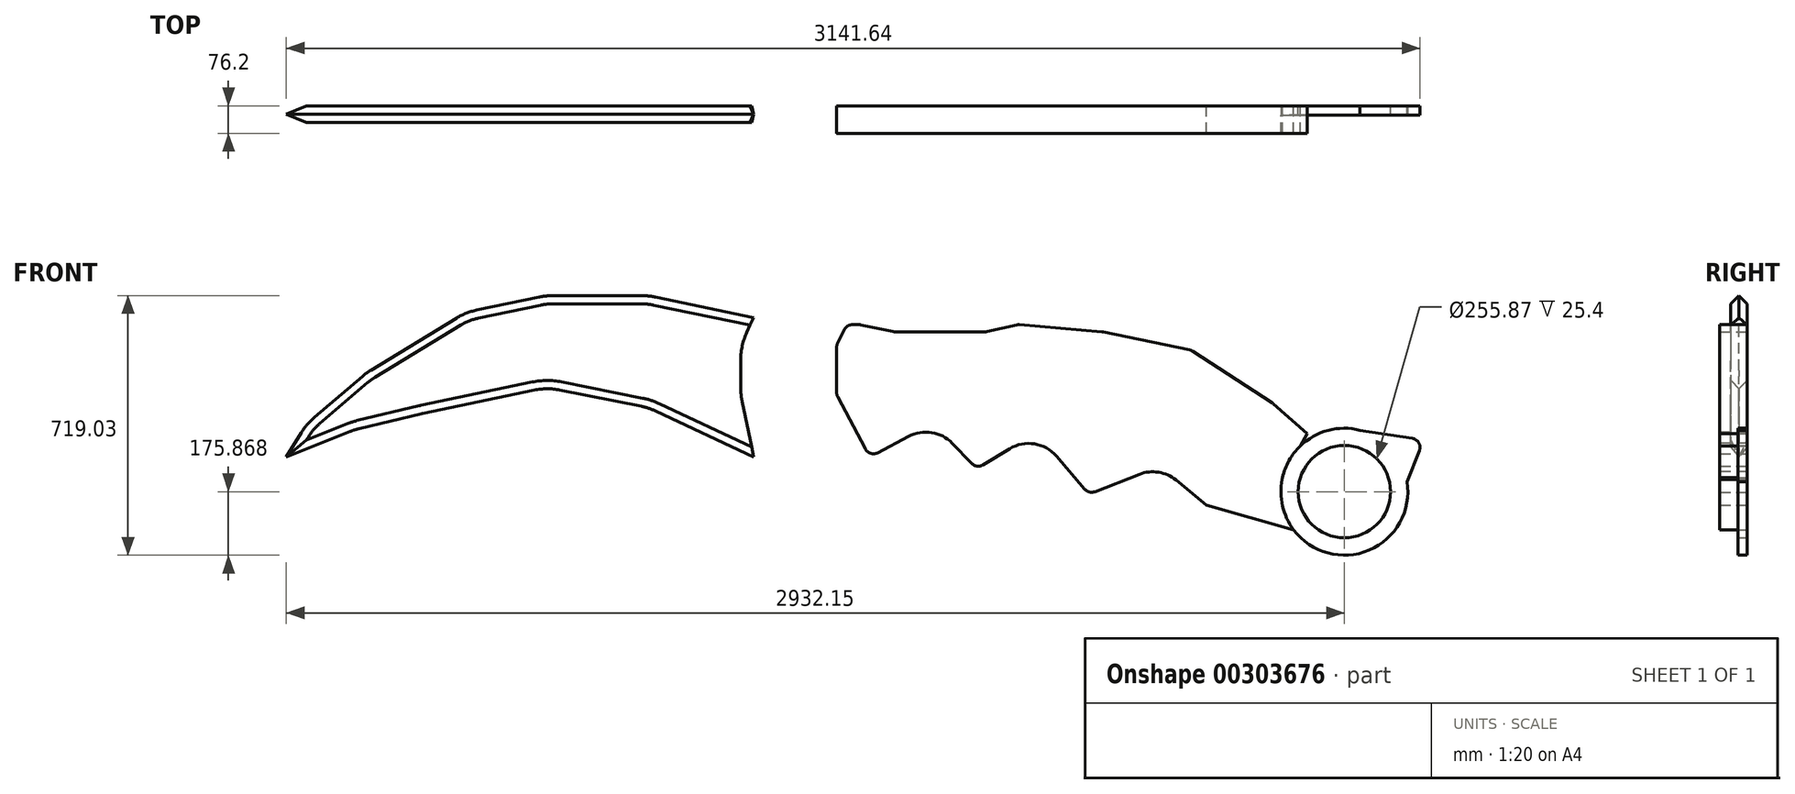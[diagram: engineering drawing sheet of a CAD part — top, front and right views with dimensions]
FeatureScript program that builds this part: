
annotation { "Feature Type Name" : "Feature", "Feature Type Description" : "" }
export const myFeature = defineFeature(function(context is Context, id is Id, definition is map)
    precondition{}
    {
        {
            var Q0;
            Q0=qCreatedBy(makeId("Front.planeOp"),FACE);
            var sketch = newSketch(context, id + "F0", { "sketchPlane" : qUnion([Q0])});
            skLineSegment(sketch, "E0", {"start": v(-453.29, 120.3) * mm, "end": v(-106.22, 192.94) * mm});
            skLineSegment(sketch, "E1", {"start": v(-106.22, 192.94) * mm, "end": v(176.28, 136.44) * mm});
            skLineSegment(sketch, "E2", {"start": v(176.28, 136.44) * mm, "end": v(466.85, 0) * mm});
            skLineSegment(sketch, "E3", {"start": v(466.85, 0) * mm, "end": v(430.81, 172.16) * mm});
            skLineSegment(sketch, "E4", {"start": v(430.81, 172.16) * mm, "end": v(430.81, 309.97) * mm});
            skLineSegment(sketch, "E5", {"start": v(430.81, 309.97) * mm, "end": v(466.85, 386.71) * mm});
            skLineSegment(sketch, "E6", {"start": v(466.85, 386.71) * mm, "end": v(176.28, 447.19) * mm});
            skLineSegment(sketch, "E7", {"start": v(176.28, 447.19) * mm, "end": v(-110.25, 447.19) * mm});
            skLineSegment(sketch, "E8", {"start": v(-110.25, 447.19) * mm, "end": v(-331, 400.99) * mm});
            skLineSegment(sketch, "E9", {"start": v(-331, 400.99) * mm, "end": v(-606.64, 233.3) * mm});
            skLineSegment(sketch, "E10", {"start": v(-606.64, 233.3) * mm, "end": v(-772.1, 92.05) * mm});
            skLineSegment(sketch, "E11", {"start": v(-453.29, 120.3) * mm, "end": v(-638.93, 75.9) * mm});
            skLineSegment(sketch, "E12", {"start": v(-638.93, 75.9) * mm, "end": v(-828.6, 0) * mm});
            skLineSegment(sketch, "E13", {"start": v(-828.6, 0) * mm, "end": v(-772.1, 92.05) * mm});
            skLineSegment(sketch, "E14", {"start": v(760.34, 366.98) * mm, "end": v(854.97, 347.29) * mm});
            skLineSegment(sketch, "E15", {"start": v(854.97, 347.29) * mm, "end": v(1111.8, 347.29) * mm});
            skLineSegment(sketch, "E16", {"start": v(1198.7, 366.98) * mm, "end": v(1111.8, 347.29) * mm});
            skLineSegment(sketch, "E17", {"start": v(1198.7, 366.98) * mm, "end": v(1433.47, 347.29) * mm});
            skLineSegment(sketch, "E18", {"start": v(1433.47, 347.29) * mm, "end": v(1678.72, 296.25) * mm});
            skLineSegment(sketch, "E19", {"start": v(1678.72, 296.25) * mm, "end": v(1905.09, 149.09) * mm});
            skLineSegment(sketch, "E20", {"start": v(1905.09, 149.09) * mm, "end": v(2000.28, 64.3) * mm});
            skLineSegment(sketch, "E21", {"start": v(2046.94, -225.32) * mm, "end": v(1721.16, -132.66) * mm});
            skLineSegment(sketch, "E22", {"start": v(1721.16, -132.66) * mm, "end": v(1591.06, -26.27) * mm});
            skLineSegment(sketch, "E23", {"start": v(1591.06, -26.27) * mm, "end": v(1395.4, -102.36) * mm});
            skLineSegment(sketch, "E24", {"start": v(1395.4, -102.36) * mm, "end": v(1249.48, 67.78) * mm});
            skLineSegment(sketch, "E25", {"start": v(1249.48, 67.78) * mm, "end": v(1084.9, -32.14) * mm});
            skLineSegment(sketch, "E26", {"start": v(1084.9, -32.14) * mm, "end": v(963.65, 93.24) * mm});
            skLineSegment(sketch, "E27", {"start": v(963.65, 93.24) * mm, "end": v(788, 0) * mm});
            skLineSegment(sketch, "E28", {"start": v(788, 0) * mm, "end": v(696.61, 172.16) * mm});
            skLineSegment(sketch, "E29", {"start": v(696.61, 172.16) * mm, "end": v(696.61, 309.97) * mm});
            skLineSegment(sketch, "E30", {"start": v(696.61, 309.97) * mm, "end": v(724.68, 366.98) * mm});
            skLineSegment(sketch, "E31", {"start": v(724.68, 366.98) * mm, "end": v(760.34, 366.98) * mm});
            skLineSegment(sketch, "E32", {"start": v(2000.28, 64.3) * mm, "end": v(1929.8, -60.84) * mm});
            skLineSegment(sketch, "E33", {"start": v(1929.8, -60.84) * mm, "end": v(2046.94, -225.32) * mm});
            skCircle(sketch, "E34", {"center": v(2103.54, -95.97) * mm, "radius": 175.87 * mm});
            skCircle(sketch, "E35", {"center": v(2103.54, -95.97) * mm, "radius": 127.93 * mm});
            skLineSegment(sketch, "E36", {"start": v(2146.97, 74.45) * mm, "end": v(2322.95, 46.97) * mm});
            skLineSegment(sketch, "E37", {"start": v(2322.95, 46.97) * mm, "end": v(2277.24, -68.42) * mm});
            skSolve(sketch);
        }
        {
            var Q0;
            Q0=makeQuery(id+"F0.imprint","IMPRINT",FACE,{"disambiguationData":[TD([[makeQuery(id+"F0.imprint","IMPRINT",EDGE,{"derivedFrom":sQuery(id+"F0.wireOp",EDGE,"E0")}),1.0]])]});
            extrude(context, id + "F1", {"entities" : qUnion([Q0]), "depth" : 45.72 * mm});
        }
        {
            var Q0;
            {var subQ0=sQuery(id+"F0.wireOp",EDGE,"E36");Q0=makeQuery(id+"F0.imprint","IMPRINT",FACE,{"disambiguationData":[TD([[makeQuery(id+"F0.imprint","IMPRINT",EDGE,{"derivedFrom":subQ0}),-1.0]])]});}
            var Q1;
            {var subQ1=sQuery(id+"F0.wireOp",EDGE,"E21");var subQ3=sQuery(id+"F0.wireOp",EDGE,"E33");var subQ5=makeQuery(id+"F0.imprint","INTERSECT",VERTEX,{"derivedFrom":[subQ1,subQ3]});Q1=makeQuery(id+"F0.imprint","IMPRINT",FACE,{"disambiguationData":[TD([[makeQuery(id+"F0.imprint","IMPRINT",EDGE,{"disambiguationData":[TD([[subQ5,-1.0]])],"derivedFrom":subQ1}),-1.0]])]});}
            var Q2;
            {var subQ1=sQuery(id+"F0.wireOp",EDGE,"E33");var subQ5=sQuery(id+"F0.wireOp",EDGE,"E21");var subQ6=makeQuery(id+"F0.imprint","INTERSECT",VERTEX,{"derivedFrom":[subQ5,subQ1]});Q2=makeQuery(id+"F0.imprint","IMPRINT",FACE,{"disambiguationData":[TD([[makeQuery(id+"F0.imprint","IMPRINT",EDGE,{"disambiguationData":[TD([[subQ6,-1.0]])],"derivedFrom":subQ5}),1.0]])]});}
            var Q3;
            {var subQ0=sQuery(id+"F0.wireOp",EDGE,"E34");var subQ1=sQuery(id+"F0.wireOp",EDGE,"E32");var subQ2=makeQuery(id+"F0.imprint","INTERSECT",VERTEX,{"disambiguationData":[OD(0.0)],"derivedFrom":[subQ1,subQ0]});Q3=makeQuery(id+"F0.imprint","IMPRINT",FACE,{"disambiguationData":[TD([[makeQuery(id+"F0.imprint","IMPRINT",EDGE,{"disambiguationData":[TD([[subQ2,-1.0]])],"derivedFrom":subQ1}),-1.0]])]});}
            extrude(context, id + "F2", {"entities" : qUnion([Q0, Q1, Q2, Q3]), "depth" : 25.4 * mm});
        }
        {
            var Q0;
            Q0=makeQuery(id+"F0.imprint","IMPRINT",FACE,{"disambiguationData":[TD([[makeQuery(id+"F0.imprint","IMPRINT",EDGE,{"derivedFrom":sQuery(id+"F0.wireOp",EDGE,"E14")}),-1.0]])]});
            extrude(context, id + "F3", {"entities" : qUnion([Q0]), "operationType" : NewBodyOperationType.ADD, "depth" : 76.2 * mm});
        }
        {
            var Q0;
            Q0=makeQuery(id+"F1.opExtrude","SWEPT_EDGE",EDGE,{"disambiguationData":[OSD([sQuery(id+"F0.wireOp",EDGE,"E11"),sQuery(id+"F0.wireOp",EDGE,"E12")])]});
            var Q1;
            Q1=makeQuery(id+"F1.opExtrude","SWEPT_EDGE",EDGE,{"disambiguationData":[OSD([sQuery(id+"F0.wireOp",EDGE,"E0"),sQuery(id+"F0.wireOp",EDGE,"E11")])]});
            var Q2;
            Q2=makeQuery(id+"F1.opExtrude","SWEPT_EDGE",EDGE,{"disambiguationData":[OSD([sQuery(id+"F0.wireOp",EDGE,"E0"),sQuery(id+"F0.wireOp",EDGE,"E1")])]});
            var Q3;
            Q3=makeQuery(id+"F1.opExtrude","SWEPT_EDGE",EDGE,{"disambiguationData":[OSD([sQuery(id+"F0.wireOp",EDGE,"E1"),sQuery(id+"F0.wireOp",EDGE,"E2")])]});
            var Q4;
            Q4=makeQuery(id+"F1.opExtrude","SWEPT_EDGE",EDGE,{"disambiguationData":[OSD([sQuery(id+"F0.wireOp",EDGE,"E3"),sQuery(id+"F0.wireOp",EDGE,"E4")])]});
            var Q5;
            Q5=makeQuery(id+"F1.opExtrude","SWEPT_EDGE",EDGE,{"disambiguationData":[OSD([sQuery(id+"F0.wireOp",EDGE,"E4"),sQuery(id+"F0.wireOp",EDGE,"E5")])]});
            var Q6;
            Q6=makeQuery(id+"F1.opExtrude","SWEPT_EDGE",EDGE,{"disambiguationData":[OSD([sQuery(id+"F0.wireOp",EDGE,"E6"),sQuery(id+"F0.wireOp",EDGE,"E7")])]});
            var Q7;
            Q7=makeQuery(id+"F1.opExtrude","SWEPT_EDGE",EDGE,{"disambiguationData":[OSD([sQuery(id+"F0.wireOp",EDGE,"E7"),sQuery(id+"F0.wireOp",EDGE,"E8")])]});
            var Q8;
            Q8=makeQuery(id+"F1.opExtrude","SWEPT_EDGE",EDGE,{"disambiguationData":[OSD([sQuery(id+"F0.wireOp",EDGE,"E8"),sQuery(id+"F0.wireOp",EDGE,"E9")])]});
            var Q9;
            Q9=makeQuery(id+"F1.opExtrude","SWEPT_EDGE",EDGE,{"disambiguationData":[OSD([sQuery(id+"F0.wireOp",EDGE,"E9"),sQuery(id+"F0.wireOp",EDGE,"E10")])]});
            var Q10;
            Q10=makeQuery(id+"F1.opExtrude","SWEPT_EDGE",EDGE,{"disambiguationData":[OSD([sQuery(id+"F0.wireOp",EDGE,"E10"),sQuery(id+"F0.wireOp",EDGE,"E13")])]});
            fillet(context, id + "F4", {"entities" : qUnion([Q0, Q1, Q2, Q3, Q4, Q5, Q6, Q7, Q8, Q9, Q10]), "radius" : 177.8 * mm, "tangentPropagation" : true, "allowEdgeOverflow" : false});
        }
        {
            var Q0;
            Q0=makeQuery(id+"F1.opExtrude","CAP_EDGE",EDGE,{"disambiguationData":[OSD([sQuery(id+"F0.wireOp",EDGE,"E2")])],"isStart":false});
            var Q1;
            {var subQ0=sQuery(id+"F0.wireOp",EDGE,"E2");var subQ1=sQuery(id+"F0.wireOp",EDGE,"E1");Q1=makeQuery(id+"F4.opFillet","BLEND_EDGE",EDGE,{"blendedFrom":[makeQuery(id+"F1.opExtrude","SWEPT_EDGE",EDGE,{"disambiguationData":[OSD([subQ1,subQ0])]}),makeQuery(id+"F1.opExtrude","CAP_FACE",FACE,{"disambiguationData":[OSD([sQuery(id+"F0.wireOp",EDGE,"E0"),subQ1,subQ0,sQuery(id+"F0.wireOp",EDGE,"E3"),sQuery(id+"F0.wireOp",EDGE,"E4"),sQuery(id+"F0.wireOp",EDGE,"E5"),sQuery(id+"F0.wireOp",EDGE,"E6"),sQuery(id+"F0.wireOp",EDGE,"E7"),sQuery(id+"F0.wireOp",EDGE,"E8"),sQuery(id+"F0.wireOp",EDGE,"E9"),sQuery(id+"F0.wireOp",EDGE,"E10"),sQuery(id+"F0.wireOp",EDGE,"E11"),sQuery(id+"F0.wireOp",EDGE,"E12"),sQuery(id+"F0.wireOp",EDGE,"E13")])],"isStart":false})],"blendedInto":[makeQuery(id+"F1.opExtrude","CAP_FACE",FACE,{"disambiguationData":[OSD([sQuery(id+"F0.wireOp",EDGE,"E0"),subQ1,subQ0,sQuery(id+"F0.wireOp",EDGE,"E3"),sQuery(id+"F0.wireOp",EDGE,"E4"),sQuery(id+"F0.wireOp",EDGE,"E5"),sQuery(id+"F0.wireOp",EDGE,"E6"),sQuery(id+"F0.wireOp",EDGE,"E7"),sQuery(id+"F0.wireOp",EDGE,"E8"),sQuery(id+"F0.wireOp",EDGE,"E9"),sQuery(id+"F0.wireOp",EDGE,"E10"),sQuery(id+"F0.wireOp",EDGE,"E11"),sQuery(id+"F0.wireOp",EDGE,"E12"),sQuery(id+"F0.wireOp",EDGE,"E13")])],"isStart":false})]});}
            var Q2;
            Q2=makeQuery(id+"F1.opExtrude","CAP_EDGE",EDGE,{"disambiguationData":[OSD([sQuery(id+"F0.wireOp",EDGE,"E1")])],"isStart":false});
            var Q3;
            Q3=makeQuery(id+"F1.opExtrude","CAP_EDGE",EDGE,{"disambiguationData":[OSD([sQuery(id+"F0.wireOp",EDGE,"E2")])],"isStart":true});
            var Q4;
            Q4=makeQuery(id+"F1.opExtrude","CAP_EDGE",EDGE,{"disambiguationData":[OSD([sQuery(id+"F0.wireOp",EDGE,"E1")])],"isStart":true});
            var Q5;
            {var subQ0=sQuery(id+"F0.wireOp",EDGE,"E2");var subQ1=sQuery(id+"F0.wireOp",EDGE,"E1");Q5=makeQuery(id+"F4.opFillet","BLEND_EDGE",EDGE,{"blendedFrom":[makeQuery(id+"F1.opExtrude","SWEPT_EDGE",EDGE,{"disambiguationData":[OSD([subQ1,subQ0])]}),makeQuery(id+"F1.opExtrude","CAP_FACE",FACE,{"disambiguationData":[OSD([sQuery(id+"F0.wireOp",EDGE,"E0"),subQ1,subQ0,sQuery(id+"F0.wireOp",EDGE,"E3"),sQuery(id+"F0.wireOp",EDGE,"E4"),sQuery(id+"F0.wireOp",EDGE,"E5"),sQuery(id+"F0.wireOp",EDGE,"E6"),sQuery(id+"F0.wireOp",EDGE,"E7"),sQuery(id+"F0.wireOp",EDGE,"E8"),sQuery(id+"F0.wireOp",EDGE,"E9"),sQuery(id+"F0.wireOp",EDGE,"E10"),sQuery(id+"F0.wireOp",EDGE,"E11"),sQuery(id+"F0.wireOp",EDGE,"E12"),sQuery(id+"F0.wireOp",EDGE,"E13")])],"isStart":true})],"blendedInto":[makeQuery(id+"F1.opExtrude","CAP_FACE",FACE,{"disambiguationData":[OSD([sQuery(id+"F0.wireOp",EDGE,"E0"),subQ1,subQ0,sQuery(id+"F0.wireOp",EDGE,"E3"),sQuery(id+"F0.wireOp",EDGE,"E4"),sQuery(id+"F0.wireOp",EDGE,"E5"),sQuery(id+"F0.wireOp",EDGE,"E6"),sQuery(id+"F0.wireOp",EDGE,"E7"),sQuery(id+"F0.wireOp",EDGE,"E8"),sQuery(id+"F0.wireOp",EDGE,"E9"),sQuery(id+"F0.wireOp",EDGE,"E10"),sQuery(id+"F0.wireOp",EDGE,"E11"),sQuery(id+"F0.wireOp",EDGE,"E12"),sQuery(id+"F0.wireOp",EDGE,"E13")])],"isStart":true})]});}
            var Q6;
            Q6=makeQuery(id+"F1.opExtrude","CAP_EDGE",EDGE,{"disambiguationData":[OSD([sQuery(id+"F0.wireOp",EDGE,"E0")])],"isStart":false});
            var Q7;
            {var subQ0=sQuery(id+"F0.wireOp",EDGE,"E1");var subQ1=sQuery(id+"F0.wireOp",EDGE,"E0");Q7=makeQuery(id+"F4.opFillet","BLEND_EDGE",EDGE,{"blendedFrom":[makeQuery(id+"F1.opExtrude","SWEPT_EDGE",EDGE,{"disambiguationData":[OSD([subQ1,subQ0])]}),makeQuery(id+"F1.opExtrude","CAP_FACE",FACE,{"disambiguationData":[OSD([subQ1,subQ0,sQuery(id+"F0.wireOp",EDGE,"E2"),sQuery(id+"F0.wireOp",EDGE,"E3"),sQuery(id+"F0.wireOp",EDGE,"E4"),sQuery(id+"F0.wireOp",EDGE,"E5"),sQuery(id+"F0.wireOp",EDGE,"E6"),sQuery(id+"F0.wireOp",EDGE,"E7"),sQuery(id+"F0.wireOp",EDGE,"E8"),sQuery(id+"F0.wireOp",EDGE,"E9"),sQuery(id+"F0.wireOp",EDGE,"E10"),sQuery(id+"F0.wireOp",EDGE,"E11"),sQuery(id+"F0.wireOp",EDGE,"E12"),sQuery(id+"F0.wireOp",EDGE,"E13")])],"isStart":true})],"blendedInto":[makeQuery(id+"F1.opExtrude","CAP_FACE",FACE,{"disambiguationData":[OSD([subQ1,subQ0,sQuery(id+"F0.wireOp",EDGE,"E2"),sQuery(id+"F0.wireOp",EDGE,"E3"),sQuery(id+"F0.wireOp",EDGE,"E4"),sQuery(id+"F0.wireOp",EDGE,"E5"),sQuery(id+"F0.wireOp",EDGE,"E6"),sQuery(id+"F0.wireOp",EDGE,"E7"),sQuery(id+"F0.wireOp",EDGE,"E8"),sQuery(id+"F0.wireOp",EDGE,"E9"),sQuery(id+"F0.wireOp",EDGE,"E10"),sQuery(id+"F0.wireOp",EDGE,"E11"),sQuery(id+"F0.wireOp",EDGE,"E12"),sQuery(id+"F0.wireOp",EDGE,"E13")])],"isStart":true})]});}
            var Q8;
            {var subQ0=sQuery(id+"F0.wireOp",EDGE,"E1");var subQ1=sQuery(id+"F0.wireOp",EDGE,"E0");Q8=makeQuery(id+"F4.opFillet","BLEND_EDGE",EDGE,{"blendedFrom":[makeQuery(id+"F1.opExtrude","SWEPT_EDGE",EDGE,{"disambiguationData":[OSD([subQ1,subQ0])]}),makeQuery(id+"F1.opExtrude","CAP_FACE",FACE,{"disambiguationData":[OSD([subQ1,subQ0,sQuery(id+"F0.wireOp",EDGE,"E2"),sQuery(id+"F0.wireOp",EDGE,"E3"),sQuery(id+"F0.wireOp",EDGE,"E4"),sQuery(id+"F0.wireOp",EDGE,"E5"),sQuery(id+"F0.wireOp",EDGE,"E6"),sQuery(id+"F0.wireOp",EDGE,"E7"),sQuery(id+"F0.wireOp",EDGE,"E8"),sQuery(id+"F0.wireOp",EDGE,"E9"),sQuery(id+"F0.wireOp",EDGE,"E10"),sQuery(id+"F0.wireOp",EDGE,"E11"),sQuery(id+"F0.wireOp",EDGE,"E12"),sQuery(id+"F0.wireOp",EDGE,"E13")])],"isStart":false})],"blendedInto":[makeQuery(id+"F1.opExtrude","CAP_FACE",FACE,{"disambiguationData":[OSD([subQ1,subQ0,sQuery(id+"F0.wireOp",EDGE,"E2"),sQuery(id+"F0.wireOp",EDGE,"E3"),sQuery(id+"F0.wireOp",EDGE,"E4"),sQuery(id+"F0.wireOp",EDGE,"E5"),sQuery(id+"F0.wireOp",EDGE,"E6"),sQuery(id+"F0.wireOp",EDGE,"E7"),sQuery(id+"F0.wireOp",EDGE,"E8"),sQuery(id+"F0.wireOp",EDGE,"E9"),sQuery(id+"F0.wireOp",EDGE,"E10"),sQuery(id+"F0.wireOp",EDGE,"E11"),sQuery(id+"F0.wireOp",EDGE,"E12"),sQuery(id+"F0.wireOp",EDGE,"E13")])],"isStart":false})]});}
            var Q9;
            Q9=makeQuery(id+"F1.opExtrude","CAP_EDGE",EDGE,{"disambiguationData":[OSD([sQuery(id+"F0.wireOp",EDGE,"E0")])],"isStart":true});
            var Q10;
            Q10=makeQuery(id+"F1.opExtrude","CAP_EDGE",EDGE,{"disambiguationData":[OSD([sQuery(id+"F0.wireOp",EDGE,"E11")])],"isStart":true});
            var Q11;
            Q11=makeQuery(id+"F1.opExtrude","CAP_EDGE",EDGE,{"disambiguationData":[OSD([sQuery(id+"F0.wireOp",EDGE,"E11")])],"isStart":false});
            var Q12;
            {var subQ0=sQuery(id+"F0.wireOp",EDGE,"E12");var subQ1=sQuery(id+"F0.wireOp",EDGE,"E11");Q12=makeQuery(id+"F4.opFillet","BLEND_EDGE",EDGE,{"blendedFrom":[makeQuery(id+"F1.opExtrude","SWEPT_EDGE",EDGE,{"disambiguationData":[OSD([subQ1,subQ0])]}),makeQuery(id+"F1.opExtrude","CAP_FACE",FACE,{"disambiguationData":[OSD([sQuery(id+"F0.wireOp",EDGE,"E0"),sQuery(id+"F0.wireOp",EDGE,"E1"),sQuery(id+"F0.wireOp",EDGE,"E2"),sQuery(id+"F0.wireOp",EDGE,"E3"),sQuery(id+"F0.wireOp",EDGE,"E4"),sQuery(id+"F0.wireOp",EDGE,"E5"),sQuery(id+"F0.wireOp",EDGE,"E6"),sQuery(id+"F0.wireOp",EDGE,"E7"),sQuery(id+"F0.wireOp",EDGE,"E8"),sQuery(id+"F0.wireOp",EDGE,"E9"),sQuery(id+"F0.wireOp",EDGE,"E10"),subQ1,subQ0,sQuery(id+"F0.wireOp",EDGE,"E13")])],"isStart":false})],"blendedInto":[makeQuery(id+"F1.opExtrude","CAP_FACE",FACE,{"disambiguationData":[OSD([sQuery(id+"F0.wireOp",EDGE,"E0"),sQuery(id+"F0.wireOp",EDGE,"E1"),sQuery(id+"F0.wireOp",EDGE,"E2"),sQuery(id+"F0.wireOp",EDGE,"E3"),sQuery(id+"F0.wireOp",EDGE,"E4"),sQuery(id+"F0.wireOp",EDGE,"E5"),sQuery(id+"F0.wireOp",EDGE,"E6"),sQuery(id+"F0.wireOp",EDGE,"E7"),sQuery(id+"F0.wireOp",EDGE,"E8"),sQuery(id+"F0.wireOp",EDGE,"E9"),sQuery(id+"F0.wireOp",EDGE,"E10"),subQ1,subQ0,sQuery(id+"F0.wireOp",EDGE,"E13")])],"isStart":false})]});}
            var Q13;
            {var subQ0=sQuery(id+"F0.wireOp",EDGE,"E12");var subQ1=sQuery(id+"F0.wireOp",EDGE,"E11");Q13=makeQuery(id+"F4.opFillet","BLEND_EDGE",EDGE,{"blendedFrom":[makeQuery(id+"F1.opExtrude","SWEPT_EDGE",EDGE,{"disambiguationData":[OSD([subQ1,subQ0])]}),makeQuery(id+"F1.opExtrude","CAP_FACE",FACE,{"disambiguationData":[OSD([sQuery(id+"F0.wireOp",EDGE,"E0"),sQuery(id+"F0.wireOp",EDGE,"E1"),sQuery(id+"F0.wireOp",EDGE,"E2"),sQuery(id+"F0.wireOp",EDGE,"E3"),sQuery(id+"F0.wireOp",EDGE,"E4"),sQuery(id+"F0.wireOp",EDGE,"E5"),sQuery(id+"F0.wireOp",EDGE,"E6"),sQuery(id+"F0.wireOp",EDGE,"E7"),sQuery(id+"F0.wireOp",EDGE,"E8"),sQuery(id+"F0.wireOp",EDGE,"E9"),sQuery(id+"F0.wireOp",EDGE,"E10"),subQ1,subQ0,sQuery(id+"F0.wireOp",EDGE,"E13")])],"isStart":true})],"blendedInto":[makeQuery(id+"F1.opExtrude","CAP_FACE",FACE,{"disambiguationData":[OSD([sQuery(id+"F0.wireOp",EDGE,"E0"),sQuery(id+"F0.wireOp",EDGE,"E1"),sQuery(id+"F0.wireOp",EDGE,"E2"),sQuery(id+"F0.wireOp",EDGE,"E3"),sQuery(id+"F0.wireOp",EDGE,"E4"),sQuery(id+"F0.wireOp",EDGE,"E5"),sQuery(id+"F0.wireOp",EDGE,"E6"),sQuery(id+"F0.wireOp",EDGE,"E7"),sQuery(id+"F0.wireOp",EDGE,"E8"),sQuery(id+"F0.wireOp",EDGE,"E9"),sQuery(id+"F0.wireOp",EDGE,"E10"),subQ1,subQ0,sQuery(id+"F0.wireOp",EDGE,"E13")])],"isStart":true})]});}
            var Q14;
            Q14=makeQuery(id+"F1.opExtrude","CAP_EDGE",EDGE,{"disambiguationData":[OSD([sQuery(id+"F0.wireOp",EDGE,"E12")])],"isStart":true});
            var Q15;
            Q15=makeQuery(id+"F1.opExtrude","CAP_EDGE",EDGE,{"disambiguationData":[OSD([sQuery(id+"F0.wireOp",EDGE,"E12")])],"isStart":false});
            var Q16;
            Q16=makeQuery(id+"F1.opExtrude","CAP_EDGE",EDGE,{"disambiguationData":[OSD([sQuery(id+"F0.wireOp",EDGE,"E13")])],"isStart":false});
            var Q17;
            Q17=makeQuery(id+"F1.opExtrude","CAP_EDGE",EDGE,{"disambiguationData":[OSD([sQuery(id+"F0.wireOp",EDGE,"E13")])],"isStart":true});
            chamfer(context, id + "F5", {"entities" : qUnion([Q0, Q1, Q2, Q3, Q4, Q5, Q6, Q7, Q8, Q9, Q10, Q11, Q12, Q13, Q14, Q15, Q16, Q17]), "chamferType" : ChamferType.OFFSET_ANGLE, "width" : 22.86 * mm, "oppositeDirection" : false, "angle" : 45 * degree, "tangentPropagation" : true});
        }
        {
            var Q0;
            Q0=makeQuery(id+"F3.opExtrude","SWEPT_EDGE",EDGE,{"disambiguationData":[OSD([sQuery(id+"F0.wireOp",EDGE,"E22"),sQuery(id+"F0.wireOp",EDGE,"E23")])]});
            var Q1;
            Q1=makeQuery(id+"F3.opExtrude","SWEPT_EDGE",EDGE,{"disambiguationData":[OSD([sQuery(id+"F0.wireOp",EDGE,"E24"),sQuery(id+"F0.wireOp",EDGE,"E25")])]});
            var Q2;
            Q2=makeQuery(id+"F3.opExtrude","SWEPT_EDGE",EDGE,{"disambiguationData":[OSD([sQuery(id+"F0.wireOp",EDGE,"E26"),sQuery(id+"F0.wireOp",EDGE,"E27")])]});
            fillet(context, id + "F6", {"entities" : qUnion([Q0, Q1, Q2]), "radius" : 101.6 * mm, "tangentPropagation" : true, "allowEdgeOverflow" : false});
        }
        {
            var Q0;
            Q0=makeQuery(id+"F3.opExtrude","SWEPT_EDGE",EDGE,{"disambiguationData":[OSD([sQuery(id+"F0.wireOp",EDGE,"E23"),sQuery(id+"F0.wireOp",EDGE,"E24")])]});
            var Q1;
            Q1=makeQuery(id+"F3.opExtrude","SWEPT_EDGE",EDGE,{"disambiguationData":[OSD([sQuery(id+"F0.wireOp",EDGE,"E25"),sQuery(id+"F0.wireOp",EDGE,"E26")])]});
            var Q2;
            Q2=makeQuery(id+"F3.opExtrude","SWEPT_EDGE",EDGE,{"disambiguationData":[OSD([sQuery(id+"F0.wireOp",EDGE,"E27"),sQuery(id+"F0.wireOp",EDGE,"E28")])]});
            fillet(context, id + "F7", {"entities" : qUnion([Q0, Q1, Q2]), "radius" : 25.4 * mm, "tangentPropagation" : true, "allowEdgeOverflow" : false});
        }
        {
            var Q0;
            Q0=makeQuery(id+"F2.opExtrude","SWEPT_EDGE",EDGE,{"disambiguationData":[OSD([sQuery(id+"F0.wireOp",EDGE,"E36"),sQuery(id+"F0.wireOp",EDGE,"E37")])]});
            var Q1;
            Q1=makeQuery(id+"F3.opExtrude","SWEPT_EDGE",EDGE,{"disambiguationData":[OSD([sQuery(id+"F0.wireOp",EDGE,"E19"),sQuery(id+"F0.wireOp",EDGE,"E20")])]});
            var Q2;
            Q2=makeQuery(id+"F3.opExtrude","SWEPT_EDGE",EDGE,{"disambiguationData":[OSD([sQuery(id+"F0.wireOp",EDGE,"E18"),sQuery(id+"F0.wireOp",EDGE,"E19")])]});
            var Q3;
            Q3=makeQuery(id+"F3.opExtrude","SWEPT_EDGE",EDGE,{"disambiguationData":[OSD([sQuery(id+"F0.wireOp",EDGE,"E17"),sQuery(id+"F0.wireOp",EDGE,"E18")])]});
            var Q4;
            Q4=makeQuery(id+"F3.opExtrude","SWEPT_EDGE",EDGE,{"disambiguationData":[OSD([sQuery(id+"F0.wireOp",EDGE,"E16"),sQuery(id+"F0.wireOp",EDGE,"E17")])]});
            var Q5;
            Q5=makeQuery(id+"F3.opExtrude","SWEPT_EDGE",EDGE,{"disambiguationData":[OSD([sQuery(id+"F0.wireOp",EDGE,"E15"),sQuery(id+"F0.wireOp",EDGE,"E16")])]});
            var Q6;
            Q6=makeQuery(id+"F3.opExtrude","SWEPT_EDGE",EDGE,{"disambiguationData":[OSD([sQuery(id+"F0.wireOp",EDGE,"E14"),sQuery(id+"F0.wireOp",EDGE,"E15")])]});
            var Q7;
            Q7=makeQuery(id+"F3.opExtrude","SWEPT_EDGE",EDGE,{"disambiguationData":[OSD([sQuery(id+"F0.wireOp",EDGE,"E14"),sQuery(id+"F0.wireOp",EDGE,"E31")])]});
            var Q8;
            Q8=makeQuery(id+"F3.opExtrude","SWEPT_EDGE",EDGE,{"disambiguationData":[OSD([sQuery(id+"F0.wireOp",EDGE,"E30"),sQuery(id+"F0.wireOp",EDGE,"E31")])]});
            var Q9;
            Q9=makeQuery(id+"F3.opExtrude","SWEPT_EDGE",EDGE,{"disambiguationData":[OSD([sQuery(id+"F0.wireOp",EDGE,"E29"),sQuery(id+"F0.wireOp",EDGE,"E30")])]});
            var Q10;
            Q10=makeQuery(id+"F3.opExtrude","SWEPT_EDGE",EDGE,{"disambiguationData":[OSD([sQuery(id+"F0.wireOp",EDGE,"E28"),sQuery(id+"F0.wireOp",EDGE,"E29")])]});
            fillet(context, id + "F8", {"entities" : qUnion([Q0, Q1, Q2, Q3, Q4, Q5, Q6, Q7, Q8, Q9, Q10]), "radius" : 25.4 * mm, "tangentPropagation" : true, "allowEdgeOverflow" : false});
        }
    });
